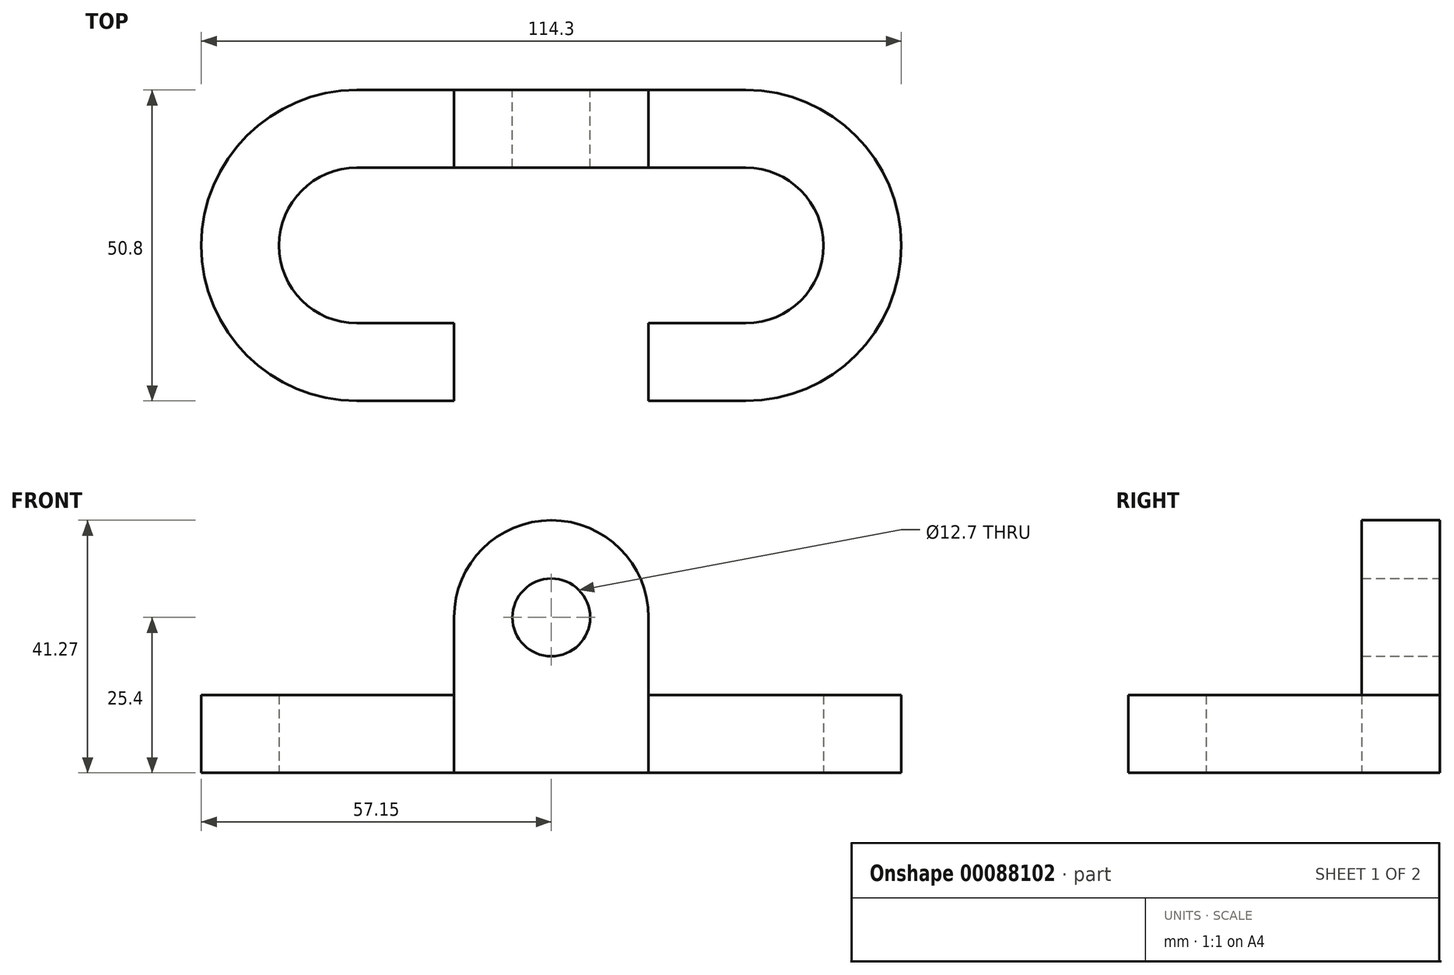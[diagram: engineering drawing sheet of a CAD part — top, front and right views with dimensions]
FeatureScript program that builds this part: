
annotation { "Feature Type Name" : "Feature", "Feature Type Description" : "" }
export const myFeature = defineFeature(function(context is Context, id is Id, definition is map)
    precondition{}
    {
        {
            var Q0;
            Q0=qCreatedBy(makeId("Top.planeOp"),FACE);
            var sketch = newSketch(context, id + "F0", { "sketchPlane" : qUnion([Q0])});
            skArc(sketch, "E0", {"start": v(0, -25.4) * mm, "mid": v(25.4, 0) * mm, "end": v(0, 25.4) * mm});
            skArc(sketch, "E1", {"start": v(0, -12.7) * mm, "mid": v(12.7, 0) * mm, "end": v(0, 12.7) * mm});
            skLineSegment(sketch, "E2", {"start": v(0, -25.4) * mm, "end": v(-15.87, -25.4) * mm});
            skLineSegment(sketch, "E3", {"start": v(-15.87, -25.4) * mm, "end": v(-15.87, -12.7) * mm});
            skLineSegment(sketch, "E4", {"start": v(-15.87, -12.7) * mm, "end": v(0, -12.7) * mm});
            skLineSegment(sketch, "E5", {"start": v(0, 12.7) * mm, "end": v(-31.75, 12.7) * mm});
            skLineSegment(sketch, "E6", {"start": v(-31.75, 12.7) * mm, "end": v(-31.75, 25.4) * mm});
            skLineSegment(sketch, "E7", {"start": v(0, 25.4) * mm, "end": v(-31.75, 25.4) * mm});
            skSolve(sketch);
        }
        {
            var Q0;
            {var subQ0=sQuery(id+"F0.wireOp",EDGE,"3gQeLjRK-feqh-ZiRs-M1Bo-GE0IdinAF737");Q0=makeQuery(id+"F0.imprint","IMPRINT",FACE,{"disambiguationData":[TD([[makeQuery(id+"F0.imprint","IMPRINT",EDGE,{"derivedFrom":subQ0}),1.0]])]});}
            var Q1;
            {var subQ0=sQuery(id+"F0.wireOp",EDGE,"E2");Q1=makeQuery(id+"F0.imprint","IMPRINT",FACE,{"disambiguationData":[TD([[makeQuery(id+"F0.imprint","IMPRINT",EDGE,{"derivedFrom":subQ0}),-1.0]])]});}
            var Q2;
            {var subQ0=sQuery(id+"F0.wireOp",EDGE,"VGncnbBv-8HQD-hPm7-KetU-IxIcI7TNnbh0");Q2=makeQuery(id+"F0.imprint","IMPRINT",FACE,{"disambiguationData":[TD([[makeQuery(id+"F0.imprint","IMPRINT",EDGE,{"derivedFrom":subQ0}),1.0]])]});}
            var Q3;
            {var subQ1=sQuery(id+"F0.wireOp",EDGE,"clHK5RPK-6nJM-tpEj-3RrV-OEgNeFLeH69J");var subQ3=sQuery(id+"F0.wireOp",EDGE,"GorKaYSy-NNG3-1fIN-QeFX-FwrOTyGfyL8j");var subQ4=makeQuery(id+"F0.imprint","INTERSECT",VERTEX,{"derivedFrom":[subQ1,subQ3]});Q3=makeQuery(id+"F0.imprint","IMPRINT",FACE,{"disambiguationData":[TD([[makeQuery(id+"F0.imprint","IMPRINT",EDGE,{"disambiguationData":[TD([[subQ4,-1.0]])],"derivedFrom":subQ1}),1.0]])]});}
            var Q4;
            {var subQ1=sQuery(id+"F0.wireOp",EDGE,"clHK5RPK-6nJM-tpEj-3RrV-OEgNeFLeH69J");var subQ3=sQuery(id+"F0.wireOp",EDGE,"D4NAhl0n-OAVm-FhwS-3p2g-RBgkbvBiMFru");var subQ4=makeQuery(id+"F0.imprint","INTERSECT",VERTEX,{"derivedFrom":[subQ1,subQ3]});Q4=makeQuery(id+"F0.imprint","IMPRINT",FACE,{"disambiguationData":[TD([[makeQuery(id+"F0.imprint","IMPRINT",EDGE,{"disambiguationData":[TD([[subQ4,1.0]])],"derivedFrom":subQ3}),-1.0]])]});}
            var Q5;
            {var subQ1=sQuery(id+"F0.wireOp",EDGE,"clHK5RPK-6nJM-tpEj-3RrV-OEgNeFLeH69J");var subQ3=sQuery(id+"F0.wireOp",EDGE,"D4NAhl0n-OAVm-FhwS-3p2g-RBgkbvBiMFru");var subQ4=makeQuery(id+"F0.imprint","INTERSECT",VERTEX,{"derivedFrom":[subQ1,subQ3]});Q5=makeQuery(id+"F0.imprint","IMPRINT",FACE,{"disambiguationData":[TD([[makeQuery(id+"F0.imprint","IMPRINT",EDGE,{"disambiguationData":[TD([[subQ4,1.0]])],"derivedFrom":subQ3}),1.0]])]});}
            var Q6;
            {var subQ5=sQuery(id+"F0.wireOp",EDGE,"ECoc7Lvu-i0xD-GHkJ-V660-dzThbDtdLFnK");Q6=makeQuery(id+"F0.imprint","IMPRINT",FACE,{"disambiguationData":[TD([[makeQuery(id+"F0.imprint","IMPRINT",EDGE,{"derivedFrom":subQ5}),1.0]])]});}
            var Q7;
            {var subQ1=sQuery(id+"F0.wireOp",EDGE,"E0");var subQ3=sQuery(id+"F0.wireOp",EDGE,"GkEZvA1Z-T089-HJYh-OUSa-vuvxDYC3xGCY");var subQ4=makeQuery(id+"F0.imprint","INTERSECT",VERTEX,{"derivedFrom":[subQ1,subQ3]});Q7=makeQuery(id+"F0.imprint","IMPRINT",FACE,{"disambiguationData":[TD([[makeQuery(id+"F0.imprint","IMPRINT",EDGE,{"disambiguationData":[TD([[subQ4,1.0]])],"derivedFrom":subQ3}),1.0]])]});}
            var Q8;
            {var subQ1=sQuery(id+"F0.wireOp",EDGE,"E0");var subQ3=sQuery(id+"F0.wireOp",EDGE,"GorKaYSy-NNG3-1fIN-QeFX-FwrOTyGfyL8j");var subQ4=makeQuery(id+"F0.imprint","INTERSECT",VERTEX,{"derivedFrom":[subQ1,subQ3]});Q8=makeQuery(id+"F0.imprint","IMPRINT",FACE,{"disambiguationData":[TD([[makeQuery(id+"F0.imprint","IMPRINT",EDGE,{"disambiguationData":[TD([[subQ4,1.0]])],"derivedFrom":subQ1}),1.0]])]});}
            var Q9;
            {var subQ5=sQuery(id+"F0.wireOp",EDGE,"E4");Q9=makeQuery(id+"F0.imprint","IMPRINT",FACE,{"disambiguationData":[TD([[makeQuery(id+"F0.imprint","IMPRINT",EDGE,{"derivedFrom":subQ5}),-1.0]])]});}
            var Q10;
            {var subQ1=sQuery(id+"F0.wireOp",EDGE,"E0");var subQ3=sQuery(id+"F0.wireOp",EDGE,"GkEZvA1Z-T089-HJYh-OUSa-vuvxDYC3xGCY");var subQ4=makeQuery(id+"F0.imprint","INTERSECT",VERTEX,{"derivedFrom":[subQ1,subQ3]});Q10=makeQuery(id+"F0.imprint","IMPRINT",FACE,{"disambiguationData":[TD([[makeQuery(id+"F0.imprint","IMPRINT",EDGE,{"disambiguationData":[TD([[subQ4,1.0]])],"derivedFrom":subQ3}),-1.0]])]});}
            var Q11;
            {var subQ4=sQuery(id+"F0.wireOp",EDGE,"E6");Q11=makeQuery(id+"F0.imprint","IMPRINT",FACE,{"disambiguationData":[TD([[makeQuery(id+"F0.imprint","IMPRINT",EDGE,{"derivedFrom":subQ4}),-1.0]])]});}
            extrude(context, id + "F1", {"entities" : qUnion([Q0, Q1, Q2, Q3, Q4, Q5, Q6, Q7, Q8, Q9, Q10, Q11]), "depth" : 12.7 * mm});
        }
        {
            var Q0;
            Q0=makeQuery(id+"F1.opExtrude","SWEPT_BODY",BODY,{"disambiguationData":[OSD([sQuery(id+"F0.wireOp",EDGE,"E0"),sQuery(id+"F0.wireOp",EDGE,"E1"),sQuery(id+"F0.wireOp",EDGE,"E2"),sQuery(id+"F0.wireOp",EDGE,"E3"),sQuery(id+"F0.wireOp",EDGE,"E4"),sQuery(id+"F0.wireOp",EDGE,"E5"),sQuery(id+"F0.wireOp",EDGE,"E6"),sQuery(id+"F0.wireOp",EDGE,"E7")])]});
            var Q1;
            Q1=makeQuery(id+"F1.opExtrude","SWEPT_FACE",FACE,{"disambiguationData":[OSD([sQuery(id+"F0.wireOp",EDGE,"E6")])]});
            mirror(context, id + "F2", {"operationType" : NewBodyOperationType.ADD, "entities" : qUnion([Q0]), "mirrorPlane" : qUnion([Q1])});
        }
        {
            var Q0;
            {var subQ0=makeQuery(id+"F1.opExtrude","SWEPT_FACE",FACE,{"disambiguationData":[OSD([sQuery(id+"F0.wireOp",EDGE,"E7")])]});Q0=makeQuery(id+"F2.boolean.opBoolean","MERGE",FACE,{"derivedFrom":[subQ0,makeQuery(id+"F2.opPattern","COPY",FACE,{"derivedFrom":subQ0,"instanceName":"1"})]});}
            var Q1;
            {var subQ0=makeQuery(id+"F1.opExtrude","SWEPT_FACE",FACE,{"disambiguationData":[OSD([sQuery(id+"F0.wireOp",EDGE,"E7")])]});Q1=makeQuery(id+"F2.boolean.opBoolean","MERGE",FACE,{"derivedFrom":[subQ0,makeQuery(id+"F2.opPattern","COPY",FACE,{"derivedFrom":subQ0,"instanceName":"1"})]});}
            var sketch = newSketch(context, id + "F3", { "sketchPlane" : qUnion([Q0, Q1])});
            skPoint(sketch, "E8", {"position": v(31.75, 0) * mm});
            skArc(sketch, "E9", {"start": v(47.62, 25.4) * mm, "mid": v(31.75, 41.28) * mm, "end": v(15.87, 25.4) * mm});
            skLineSegment(sketch, "E10", {"start": v(15.87, 25.4) * mm, "end": v(15.87, 12.7) * mm});
            skLineSegment(sketch, "E11", {"start": v(47.62, 25.4) * mm, "end": v(47.62, 12.7) * mm});
            skCircle(sketch, "E12", {"center": v(31.75, 25.4) * mm, "radius": 6.35 * mm});
            skSolve(sketch);
        }
        {
            var Q0;
            Q0=makeQuery(id+"F3.imprint","IMPRINT",FACE,{"disambiguationData":[TD([[makeQuery(id+"F3.imprint","IMPRINT",EDGE,{"derivedFrom":sQuery(id+"F3.wireOp",EDGE,"E9")}),1.0]])]});
            var Q1;
            {var subQ0=makeQuery(id+"F1.opExtrude","SWEPT_FACE",FACE,{"disambiguationData":[OSD([sQuery(id+"F0.wireOp",EDGE,"E5")])]});Q1=makeQuery(id+"F2.boolean.opBoolean","MERGE",FACE,{"derivedFrom":[subQ0,makeQuery(id+"F2.opPattern","COPY",FACE,{"derivedFrom":subQ0,"instanceName":"1"})]});}
            extrude(context, id + "F4", {"entities" : qUnion([Q0]), "operationType" : NewBodyOperationType.ADD, "endBound" : BoundingType.UP_TO_SURFACE, "oppositeDirection" : true, "endBoundEntityFace" : qUnion([Q1]), "depth" : 25.4 * mm});
        }
    });
